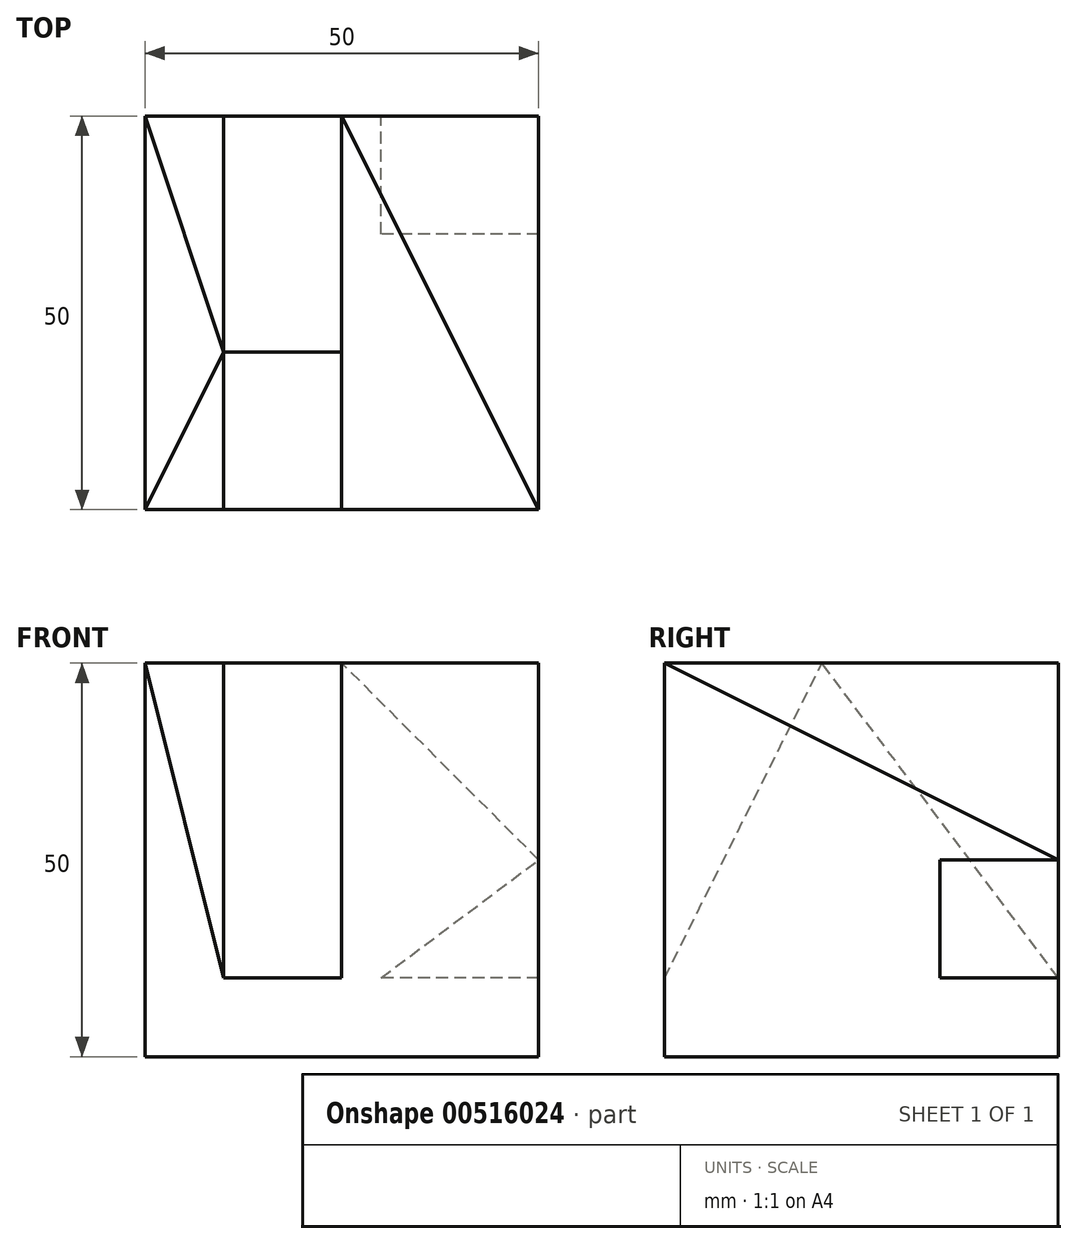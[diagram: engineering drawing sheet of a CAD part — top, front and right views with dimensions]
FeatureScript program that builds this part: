
annotation { "Feature Type Name" : "Feature", "Feature Type Description" : "" }
export const myFeature = defineFeature(function(context is Context, id is Id, definition is map)
    precondition{}
    {
        {
            var Q0;
            Q0=qCreatedBy(makeId("Top.planeOp"),FACE);
            var sketch = newSketch(context, id + "F0", { "sketchPlane" : qUnion([Q0])});
            skLineSegment(sketch, "E0.bottom", {"start": v(0, 0) * mm, "end": v(50, 0) * mm});
            skLineSegment(sketch, "E0.top", {"start": v(0, 50) * mm, "end": v(50, 50) * mm});
            skLineSegment(sketch, "E0.left", {"start": v(0, 0) * mm, "end": v(0, 50) * mm});
            skLineSegment(sketch, "E0.right", {"start": v(50, 0) * mm, "end": v(50, 50) * mm});
            skSolve(sketch);
        }
        {
            var Q0;
            Q0=makeQuery(id+"F0.imprint","IMPRINT",FACE,{"disambiguationData":[TD([[makeQuery(id+"F0.imprint","IMPRINT",EDGE,{"derivedFrom":sQuery(id+"F0.wireOp",EDGE,"E0.bottom")}),1.0]])]});
            extrude(context, id + "F1", {"entities" : qUnion([Q0]), "depth" : 50 * mm, "offsetDistance" : 25 * mm});
        }
        {
            var Q0;
            Q0=makeQuery(id+"F1.opExtrude","SWEPT_FACE",FACE,{"disambiguationData":[OSD([sQuery(id+"F0.wireOp",EDGE,"E0.top")])]});
            var sketch = newSketch(context, id + "F2", { "sketchPlane" : qUnion([Q0])});
            skLineSegment(sketch, "E1", {"start": v(-50, 10) * mm, "end": v(-30, 10) * mm});
            skLineSegment(sketch, "E2", {"start": v(-30, 10) * mm, "end": v(-50, 25) * mm});
            skSolve(sketch);
        }
        {
            var Q0;
            Q0 = qSketchRegion(id + "F2", true);
            var Q1;
            {var subQ0=sQuery(id+"F2.wireOp",EDGE,"E1");Q1=makeQuery(id+"F2.imprint","IMPRINT",FACE,{"disambiguationData":[TD([[makeQuery(id+"F2.imprint","IMPRINT",EDGE,{"derivedFrom":subQ0}),1.0]])]});}
            extrude(context, id + "F3", {"entities" : qUnion([Q0, Q1]), "operationType" : NewBodyOperationType.REMOVE, "oppositeDirection" : true, "depth" : 15 * mm, "offsetDistance" : 25 * mm});
        }
        {
            var Q0;
            Q0=makeQuery(id+"F1.opExtrude","SWEPT_FACE",FACE,{"disambiguationData":[OSD([sQuery(id+"F0.wireOp",EDGE,"E0.right")])]});
            var sketch = newSketch(context, id + "F4", { "sketchPlane" : qUnion([Q0])});
            skLineSegment(sketch, "E3", {"start": v(0, 50) * mm, "end": v(50, 25) * mm});
            skSolve(sketch);
        }
        {
            var Q0;
            Q0=makeQuery(id+"F1.opExtrude","SWEPT_FACE",FACE,{"disambiguationData":[OSD([sQuery(id+"F0.wireOp",EDGE,"E0.top")])]});
            var sketch = newSketch(context, id + "F5", { "sketchPlane" : qUnion([Q0])});
            skLineSegment(sketch, "E4", {"start": v(-50, 25) * mm, "end": v(-25, 50) * mm});
            skSolve(sketch);
        }
        {
            var Q0;
            Q0=makeQuery(id+"F4.imprint","IMPRINT",FACE,{"disambiguationData":[TD([[makeQuery(id+"F4.imprint","IMPRINT",EDGE,{"derivedFrom":sQuery(id+"F4.wireOp",EDGE,"E3")}),1.0]])]});
            var Q1;
            Q1=sQuery(id+"F5.wireOp",EDGE,"E4");
            sweep(context, id + "F6", {"operationType" : NewBodyOperationType.REMOVE, "profiles" : qUnion([Q0]), "path" : qUnion([Q1])});
        }
        {
            var Q0;
            Q0=makeQuery(id+"F1.opExtrude","SWEPT_FACE",FACE,{"disambiguationData":[OSD([sQuery(id+"F0.wireOp",EDGE,"E0.left")])]});
            var sketch = newSketch(context, id + "F7", { "sketchPlane" : qUnion([Q0])});
            skLineSegment(sketch, "E5", {"start": v(-50, 10) * mm, "end": v(-20, 50) * mm});
            skLineSegment(sketch, "E6", {"start": v(-20, 50) * mm, "end": v(0, 10) * mm});
            skSolve(sketch);
        }
        {
            var Q0;
            Q0=makeQuery(id+"F1.opExtrude","SWEPT_FACE",FACE,{"disambiguationData":[OSD([sQuery(id+"F0.wireOp",EDGE,"E0.bottom")])]});
            var sketch = newSketch(context, id + "F8", { "sketchPlane" : qUnion([Q0])});
            skLineSegment(sketch, "E7.bottom", {"start": v(10, 50) * mm, "end": v(25, 50) * mm});
            skLineSegment(sketch, "E7.top", {"start": v(10, 10) * mm, "end": v(25, 10) * mm});
            skLineSegment(sketch, "E7.left", {"start": v(10, 50) * mm, "end": v(10, 10) * mm});
            skLineSegment(sketch, "E7.right", {"start": v(25, 50) * mm, "end": v(25, 10) * mm});
            skSolve(sketch);
        }
        {
            var Q0;
            Q0=makeQuery(id+"F8.imprint","IMPRINT",FACE,{"disambiguationData":[TD([[makeQuery(id+"F8.imprint","IMPRINT",EDGE,{"derivedFrom":sQuery(id+"F8.wireOp",EDGE,"E7.bottom")}),-1.0]])]});
            var Q1;
            Q1=sQuery(id+"F7.wireOp",EDGE,"E6");
            sweep(context, id + "F9", {"operationType" : NewBodyOperationType.REMOVE, "profiles" : qUnion([Q0]), "path" : qUnion([Q1])});
        }
        {
            var Q0;
            Q0=makeQuery(id+"F1.opExtrude","SWEPT_FACE",FACE,{"disambiguationData":[OSD([sQuery(id+"F0.wireOp",EDGE,"E0.top")])]});
            var sketch = newSketch(context, id + "F10", { "sketchPlane" : qUnion([Q0])});
            skLineSegment(sketch, "E8.bottom", {"start": v(-25, 50) * mm, "end": v(-10, 50) * mm});
            skLineSegment(sketch, "E8.top", {"start": v(-25, 10) * mm, "end": v(-10, 10) * mm});
            skLineSegment(sketch, "E8.left", {"start": v(-25, 50) * mm, "end": v(-25, 10) * mm});
            skLineSegment(sketch, "E8.right", {"start": v(-10, 50) * mm, "end": v(-10, 10) * mm});
            skSolve(sketch);
        }
        {
            var Q0;
            Q0=makeQuery(id+"F10.imprint","IMPRINT",FACE,{"disambiguationData":[TD([[makeQuery(id+"F10.imprint","IMPRINT",EDGE,{"derivedFrom":sQuery(id+"F10.wireOp",EDGE,"E8.bottom")}),1.0]])]});
            var Q1;
            Q1=sQuery(id+"F7.wireOp",EDGE,"E5");
            sweep(context, id + "F11", {"operationType" : NewBodyOperationType.REMOVE, "profiles" : qUnion([Q0]), "path" : qUnion([Q1])});
        }
        {
            var Q0;
            {var subQ1=sQuery(id+"F0.wireOp",EDGE,"E0.left");var subQ3=sQuery(id+"F0.wireOp",EDGE,"E0.top");var subQ4=sQuery(id+"F0.wireOp",EDGE,"E0.bottom");Q0=makeQuery(id+"F11.boolean.opBoolean","SPLIT",FACE,{"disambiguationData":[TD([makeQuery(id+"F1.opExtrude","SWEPT_FACE",FACE,{"disambiguationData":[OSD([subQ1])]})])],"derivedFrom":makeQuery(id+"F1.opExtrude","CAP_FACE",FACE,{"disambiguationData":[OSD([subQ4,subQ3,subQ1,sQuery(id+"F0.wireOp",EDGE,"E0.right")])],"isStart":false})});}
            var sketch = newSketch(context, id + "F12", { "sketchPlane" : qUnion([Q0])});
            skLineSegment(sketch, "E9", {"start": v(10, 20) * mm, "end": v(0, 0) * mm});
            skSolve(sketch);
        }
        {
            var Q0;
            Q0=makeQuery(id+"F9.boolean.opBoolean","COPY",FACE,{"derivedFrom":makeQuery(id+"F9.opSweep","SWEPT_FACE",FACE,{"disambiguationData":[OSD([sQuery(id+"F7.wireOp",EDGE,"E6"),sQuery(id+"F8.wireOp",EDGE,"E7.left")])]})});
            var Q1;
            Q1=sQuery(id+"F12.wireOp",EDGE,"E9");
            sweep(context, id + "F13", {"operationType" : NewBodyOperationType.REMOVE, "profiles" : qUnion([Q0]), "path" : qUnion([Q1])});
        }
        {
            var Q0;
            {var subQ1=sQuery(id+"F0.wireOp",EDGE,"E0.left");var subQ3=sQuery(id+"F0.wireOp",EDGE,"E0.top");var subQ4=sQuery(id+"F0.wireOp",EDGE,"E0.bottom");Q0=makeQuery(id+"F11.boolean.opBoolean","SPLIT",FACE,{"disambiguationData":[TD([makeQuery(id+"F1.opExtrude","SWEPT_FACE",FACE,{"disambiguationData":[OSD([subQ1])]})])],"derivedFrom":makeQuery(id+"F1.opExtrude","CAP_FACE",FACE,{"disambiguationData":[OSD([subQ4,subQ3,subQ1,sQuery(id+"F0.wireOp",EDGE,"E0.right")])],"isStart":false})});}
            var sketch = newSketch(context, id + "F14", { "sketchPlane" : qUnion([Q0])});
            skLineSegment(sketch, "E10", {"start": v(10, 20) * mm, "end": v(0, 50) * mm});
            skSolve(sketch);
        }
        {
            var Q0;
            Q0=makeQuery(id+"F11.boolean.opBoolean","COPY",FACE,{"derivedFrom":makeQuery(id+"F11.opSweep","SWEPT_FACE",FACE,{"disambiguationData":[OSD([sQuery(id+"F7.wireOp",EDGE,"E5"),sQuery(id+"F10.wireOp",EDGE,"E8.right")])]})});
            var Q1;
            Q1=sQuery(id+"F14.wireOp",EDGE,"E10");
            sweep(context, id + "F15", {"operationType" : NewBodyOperationType.REMOVE, "profiles" : qUnion([Q0]), "path" : qUnion([Q1])});
        }
    });
